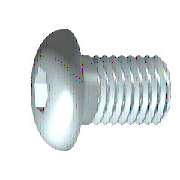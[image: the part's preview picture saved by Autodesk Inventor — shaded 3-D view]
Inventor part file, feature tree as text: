
AUTODESK INVENTOR PART (.ipt)
format: ipt  version: 2013 (Build 170138000, 138)  size: 192,512 bytes
history: native  units: mm (DEFAULTED — no unit token found)
features: sketch x2, extrude x1, plane x1, fillet x1
ambient origin geometry x7: Origin, YZ Plane, XY Plane, X Axis, Y Axis, Z Axis, Center Point
bodies: Solid1 (feature_tree), Body (feature_tree)
feature tree (5):
  extrude  "Slot"  Depth=1.59014mm
  plane  "Work Plane1"
  fillet  "Fillet2"  Radius=2.2098mm
  sketch  "Sketch1"  dims[d1=11.10976mm d2=1.59014mm d3=2.2098mm]
  sketch  "Sketch2"  dims[d4=1.3208mm d5=60.0deg d6=4.1656mm d7=4.1656mm d8=2.756963mm d9=7.9248mm d10=90.0deg d11=10.0mm d12=0.0mm d13=11.10976mm d14=0.0mm d15=0.486918mm d16=0.486918mm d17=1.9558mm d19=0.0mm d26=12.7mm d27=45.0deg d28=0.0mm d29=0.0mm d30=0.1mm]
